# Revit family: Приточная система с водяным нагревом водяным охлаждением
name_source: partatom
category: Оборудование
units: mm (PartAtom-declared; Revit-internal decimal feet)

## family parameters
Всегда вертикально = Да
Классификация = Нет
На основе рабочей плоскости = Нет
Общий = Нет
При загрузке вырезать с полостями = Нет
Размер круглого соединителя = Использовать диаметр
Тип детали = Нормальный
Точка принадлежности помещению = Нет

## types (16) — shared parameters
ADSK_Напряжение = 380 В
ADSK_Свободный напор воздуха = 400.0 Па
Длина гибкой встаки = 125 мм
Длина клапана FC = 120 мм
Слив конденсата = 15 мм
zero-valued in all types: Длина секции испарителя CF, Отметка по умолчанию, Подключение испарителя E

## per-type parameters (varying)
| type | ADSK_Масса | ADSK_Обозначение | ADSK_Размер_Высота | ADSK_Размер_Ширина | ADSK_Расход теплоносителя | ADSK_Расход холодоносителя | ADSK_Частота вращения двигателя | Высота ГВ | Высота рамы | Ширина ГВ |
| 1А | 244 | П3.1 | 440 мм | 850 мм | 0.7 кубический метр в час | 0.7 кубический метр в час | 2835 | 440 мм | 0 мм | 850 мм |
| 2А | 285 | П3.2 | 505 мм | 980 мм | 1.4 кубический метр в час | 1.5 кубический метр в час | 2805 | 505 мм | 0 мм | 980 мм |
| 16B | 1619 | П3.16 | 2580 мм | 2580 мм | 18.8 кубический метр в час | 19.6 кубический метр в час | 1460 | 2580 мм | 120 мм | 2580 мм |
| 3A | 343 | П3.3 | 695 мм | 1080 мм | 2.0 кубический метр в час | 2.0 кубический метр в час | 2830 | 695 мм | 120 мм | 1080 мм |
| 4A | 306 | П3.4 | 695 мм | 1360 мм | 2.6 кубический метр в час | 2.6 кубический метр в час | 2880 | 695 мм | 120 мм | 1360 мм |
| 5A | 429 | П3.5 | 803 мм | 1360 мм | 3.1 кубический метр в час | 3.2 кубический метр в час | 2880 | 803 мм | 120 мм | 1360 мм |
| 6A | 482 | П3.6 | 803 мм | 1580 мм | 3.7 кубический метр в час | 3.8 кубический метр в час | 2905 | 803 мм | 120 мм | 1580 мм |
| 7A | 531 | П3.7 | 990 мм | 1580 мм | 4.3 кубический метр в час | 4.5 кубический метр в час | 2945 | 990 мм | 120 мм | 1580 мм |
| 8A | 637 | П3.8 | 990 мм | 1950 мм | 5.1 кубический метр в час | 5.4 кубический метр в час | 2945 | 990 мм | 120 мм | 1950 мм |
| 9A | 736 | П3.9 | 1095 мм | 2160 мм | 6.3 кубический метр в час | 6.5 кубический метр в час | 1455 | 1095 мм | 120 мм | 2160 мм |
| 10B | 872 | П3.10 | 1360 мм | 2040 мм | 7.4 кубический метр в час | 7.6 кубический метр в час | 1460 | 1360 мм | 120 мм | 2040 мм |
| 12B | 1040 | П3.12 | 1680 мм | 2040 мм | 10.2 кубический метр в час | 10.2 кубический метр в час | 1465 | 1680 мм | 120 мм | 2040 мм |
| 11B | 1062.8 | П3.11 | 1360 мм | 2580 мм | 9.7 кубический метр в час | 10.1 кубический метр в час | 1465 | 1360 мм | 120 мм | 2580 мм |
| 13B | 1129 | П3.13 | 2040 мм | 2040 мм | 11.4 кубический метр в час | 11.9 кубический метр в час | 1465 | 2040 мм | 120 мм | 2040 мм |
| 14B | 1222 | П3.14 | 1680 мм | 2580 мм | 12.5 кубический метр в час | 130.9 кубический метр в час | 1465 | 1680 мм | 120 мм | 2580 мм |
| 15B | 1386 | П3.15 | 2040 мм | 2580 мм | 13.6 кубический метр в час | 14.2 кубический метр в час | 1470 | 2040 мм | 120 мм | 2580 мм |
